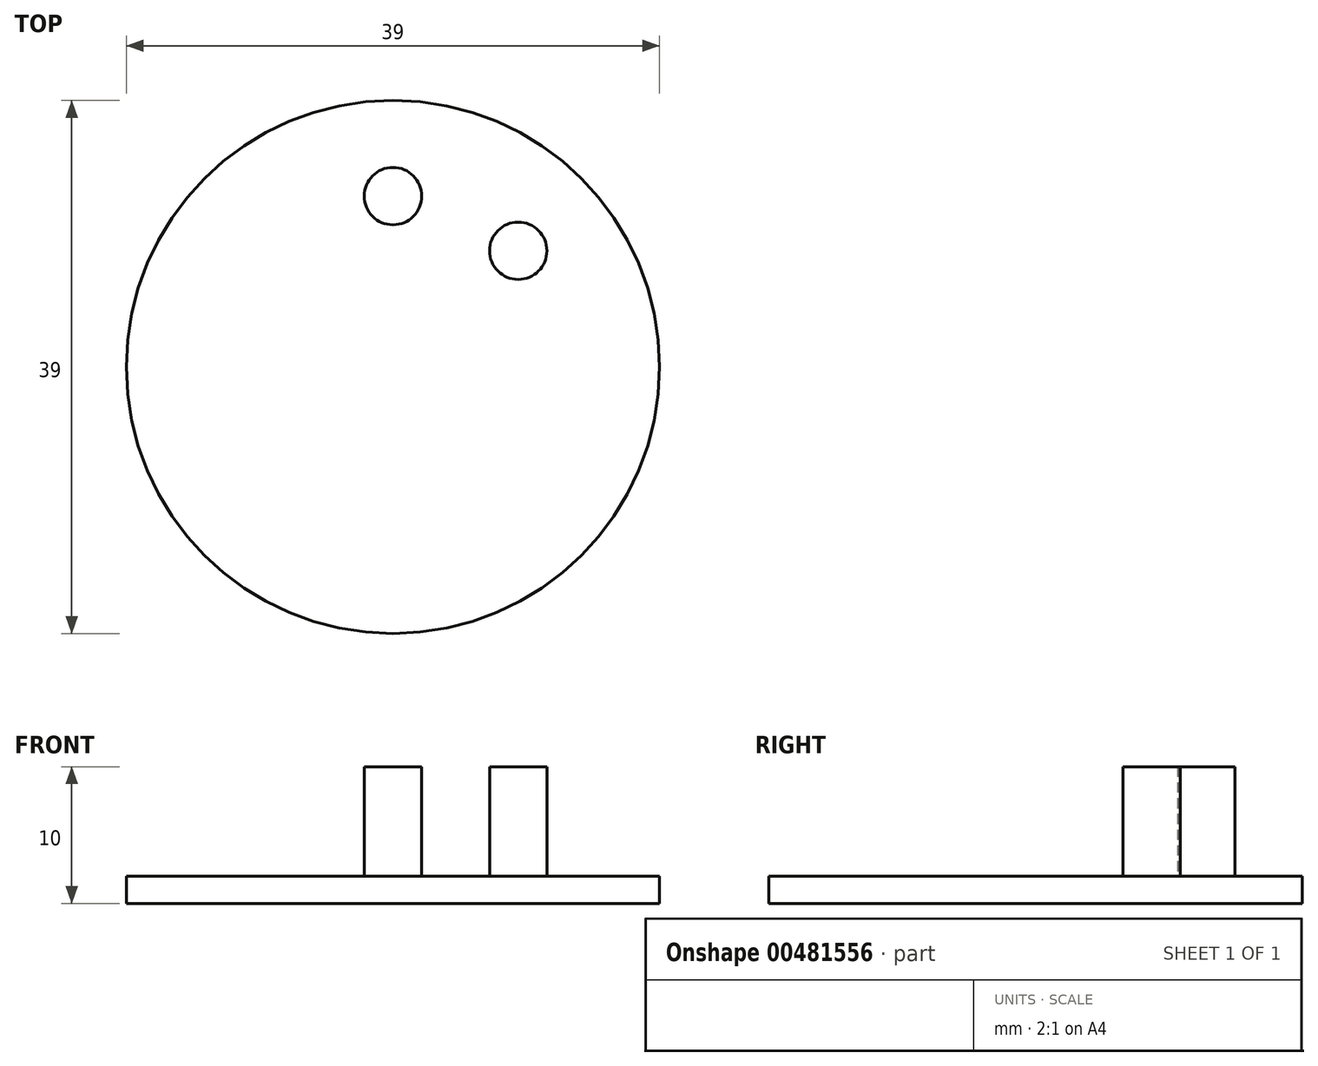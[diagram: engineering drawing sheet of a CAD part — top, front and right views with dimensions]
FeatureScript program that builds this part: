
annotation { "Feature Type Name" : "Feature", "Feature Type Description" : "" }
export const myFeature = defineFeature(function(context is Context, id is Id, definition is map)
    precondition{}
    {
        {
            var Q0;
            Q0=qCreatedBy(makeId("Top.planeOp"),FACE);
            var sketch = newSketch(context, id + "F0", { "sketchPlane" : qUnion([Q0])});
            skCircle(sketch, "E0", {"center": v(0, 0) * mm, "radius": 12.5 * mm, "construction": true});
            skCircle(sketch, "E1", {"center": v(0, 12.5) * mm, "radius": 5 * mm, "construction": true});
            skCircle(sketch, "E2", {"center": v(9.17, 8.5) * mm, "radius": 5 * mm, "construction": true});
            skCircle(sketch, "E3", {"center": v(0, 0) * mm, "radius": 7.5 * mm, "construction": true});
            skCircle(sketch, "E4", {"center": v(0, 0) * mm, "radius": 19.5 * mm});
            skCircle(sketch, "E5", {"center": v(0, 12.5) * mm, "radius": 2.1 * mm});
            skCircle(sketch, "E6", {"center": v(9.17, 8.5) * mm, "radius": 2.1 * mm});
            skSolve(sketch);
        }
        {
            var Q0;
            Q0=makeQuery(id+"F0.imprint","IMPRINT",FACE,{"disambiguationData":[TD([[makeQuery(id+"F0.imprint","IMPRINT",EDGE,{"derivedFrom":sQuery(id+"F0.wireOp",EDGE,"E4")}),1.0]])]});
            extrude(context, id + "F1", {"entities" : qUnion([Q0]), "depth" : 2 * mm});
        }
        {
            var Q0;
            Q0=makeQuery(id+"F0.imprint","IMPRINT",FACE,{"disambiguationData":[TD([[makeQuery(id+"F0.imprint","IMPRINT",EDGE,{"derivedFrom":sQuery(id+"F0.wireOp",EDGE,"E5")}),1.0]])]});
            var Q1;
            Q1=makeQuery(id+"F0.imprint","IMPRINT",FACE,{"disambiguationData":[TD([[makeQuery(id+"F0.imprint","IMPRINT",EDGE,{"derivedFrom":sQuery(id+"F0.wireOp",EDGE,"E6")}),1.0]])]});
            extrude(context, id + "F2", {"entities" : qUnion([Q0, Q1]), "operationType" : NewBodyOperationType.ADD, "depth" : 10 * mm});
        }
    });
